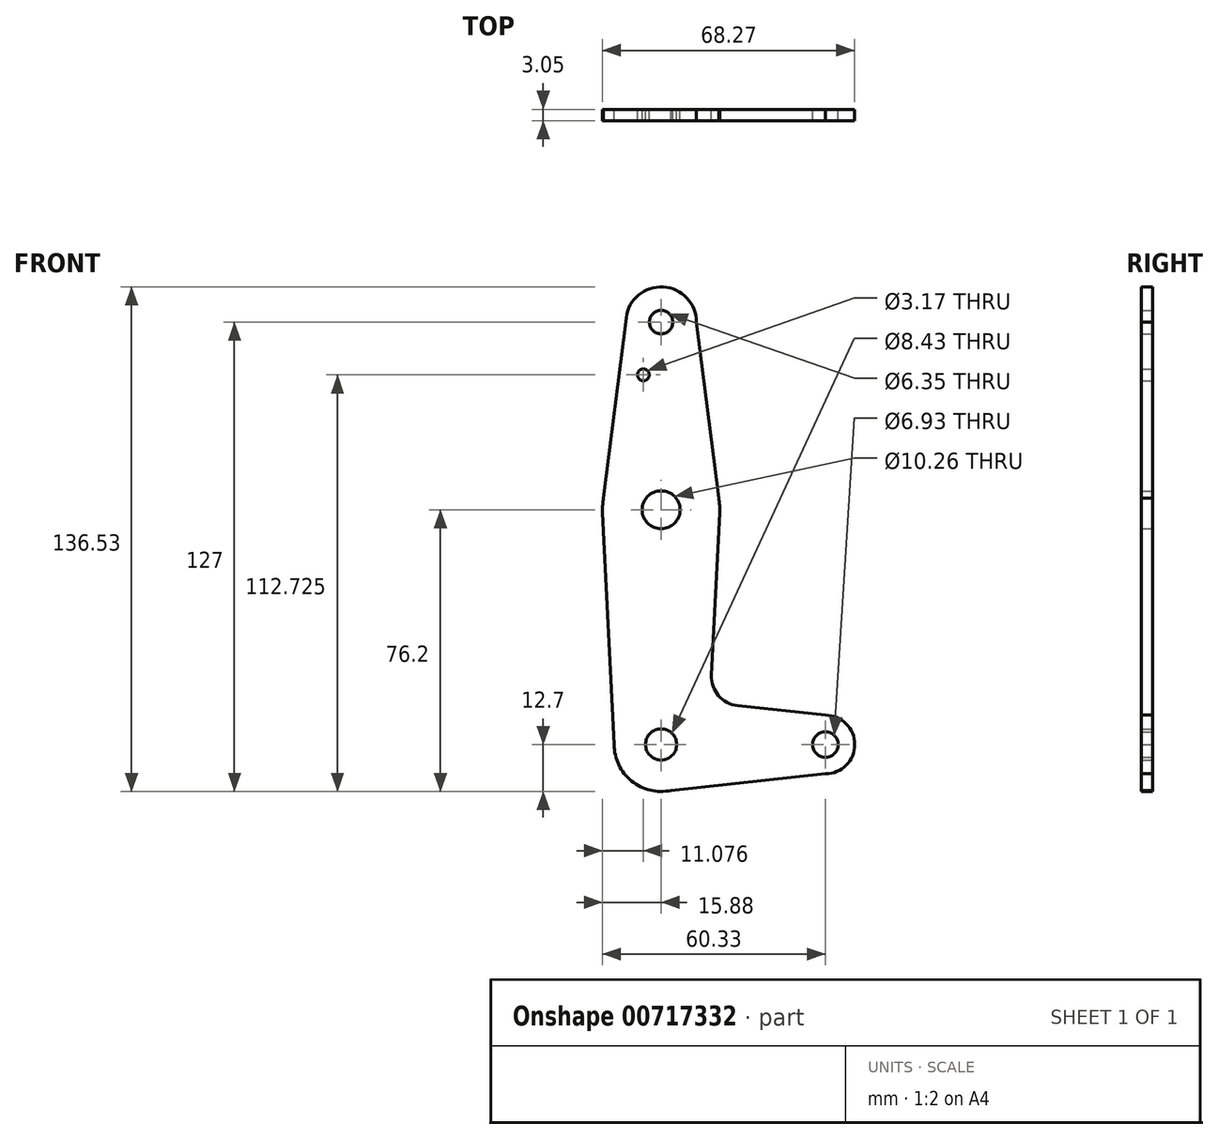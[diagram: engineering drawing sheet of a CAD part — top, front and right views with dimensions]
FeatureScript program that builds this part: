
annotation { "Feature Type Name" : "Feature", "Feature Type Description" : "" }
export const myFeature = defineFeature(function(context is Context, id is Id, definition is map)
    precondition{}
    {
        {
            var Q0;
            Q0=qCreatedBy(makeId("Front.planeOp"),FACE);
            var sketch = newSketch(context, id + "F0", { "sketchPlane" : qUnion([Q0])});
            skLineSegment(sketch, "E0", {"start": v(0, 0) * mm, "end": v(0, 114.3) * mm, "construction": true});
            skLineSegment(sketch, "E1", {"start": v(0, 0) * mm, "end": v(44.45, 0) * mm, "construction": true});
            skArc(sketch, "E2", {"start": v(0, 12.7) * mm, "mid": v(-1.35, -12.63) * mm, "end": v(2.7, 12.41) * mm});
            skCircle(sketch, "E3", {"center": v(44.45, 0) * mm, "radius": 7.94 * mm});
            skCircle(sketch, "E4", {"center": v(0, 63.5) * mm, "radius": 15.88 * mm});
            skCircle(sketch, "E5", {"center": v(0, 114.3) * mm, "radius": 9.53 * mm});
            skLineSegment(sketch, "E6", {"start": v(0, -12.7) * mm, "end": v(44.45, -7.94) * mm});
            skLineSegment(sketch, "E7", {"start": v(0, 12.7) * mm, "end": v(2.7, 12.41) * mm});
            skLineSegment(sketch, "E8", {"start": v(-12.7, 0) * mm, "end": v(-15.85, 62.7) * mm});
            skLineSegment(sketch, "E9", {"start": v(13.65, 18.78) * mm, "end": v(15.85, 62.7) * mm});
            skLineSegment(sketch, "E10", {"start": v(-15.85, 64.3) * mm, "end": v(-9.45, 115.48) * mm});
            skLineSegment(sketch, "E11", {"start": v(15.85, 64.3) * mm, "end": v(9.52, 114.3) * mm});
            skCircle(sketch, "E12", {"center": v(0, 114.3) * mm, "radius": 3.18 * mm});
            skCircle(sketch, "E13", {"center": v(0, 63.5) * mm, "radius": 5.13 * mm});
            skCircle(sketch, "E14", {"center": v(0, 0) * mm, "radius": 4.21 * mm});
            skCircle(sketch, "E15", {"center": v(44.45, 0) * mm, "radius": 3.46 * mm});
            skLineSegment(sketch, "E16.trimOffspring", {"start": v(20.74, 10.48) * mm, "end": v(44.45, 7.94) * mm});
            skPoint(sketch, "E17.visualSharp", {"position": v(13.27, 11.28) * mm});
            skArc(sketch, "E17.filletArc", {"start": v(13.65, 18.78) * mm, "mid": v(15.54, 13.22) * mm, "end": v(20.74, 10.48) * mm});
            skCircle(sketch, "E18", {"center": v(-4.8, 100.03) * mm, "radius": 1.59 * mm});
            skSolve(sketch);
        }
        {
            var Q0;
            Q0 = qSketchRegion(id + "F0", true);
            extrude(context, id + "F1", {"entities" : qUnion([Q0]), "depth" : 3.05 * mm, "offsetDistance" : 25.4 * mm});
        }
    });
